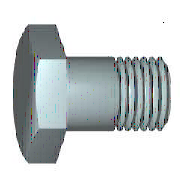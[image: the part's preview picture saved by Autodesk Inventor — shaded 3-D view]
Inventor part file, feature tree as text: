
AUTODESK INVENTOR PART (.ipt)
format: ipt  version: 2022.1 (Build 261234000, 234)  size: 190,976 bytes
history: native  units: mm (DEFAULTED — no unit token found)
features: sketch x3, other x1, extrude x1, chamfer x1, plane x1
ambient origin geometry x7: Origin, YZ Plane, XZ Plane, X Axis, Y Axis, Z Axis, Center Point
bodies: Solid1 (feature_tree)
feature tree (7):
  other  "Cuerpo"
  extrude  "Cabeza"  Depth=34.0mm
  chamfer  "Chaflán1"  Distance=8.2mm
  plane  "Work Plane1"
  sketch  "Boceto1"  dims[d0=90.0mm d1=34.0mm]
  sketch  "Boceto2"  dims[d2=14.0mm]
  sketch  "Boceto4"  dims[d12=90.0deg d3=8.2mm d4=0.0mm d5=30.0deg d21=90.0deg d6=1.2269mm d7=1.227mm d8=0.0mm d9=0.6001mm d10=19.37mm d11=21.0mm d13=1.227mm d14=14.0mm d15=34.0mm d16=0.0mm d19=21.0mm d55=45.0deg d57=0.0mm d58=0.0mm]
